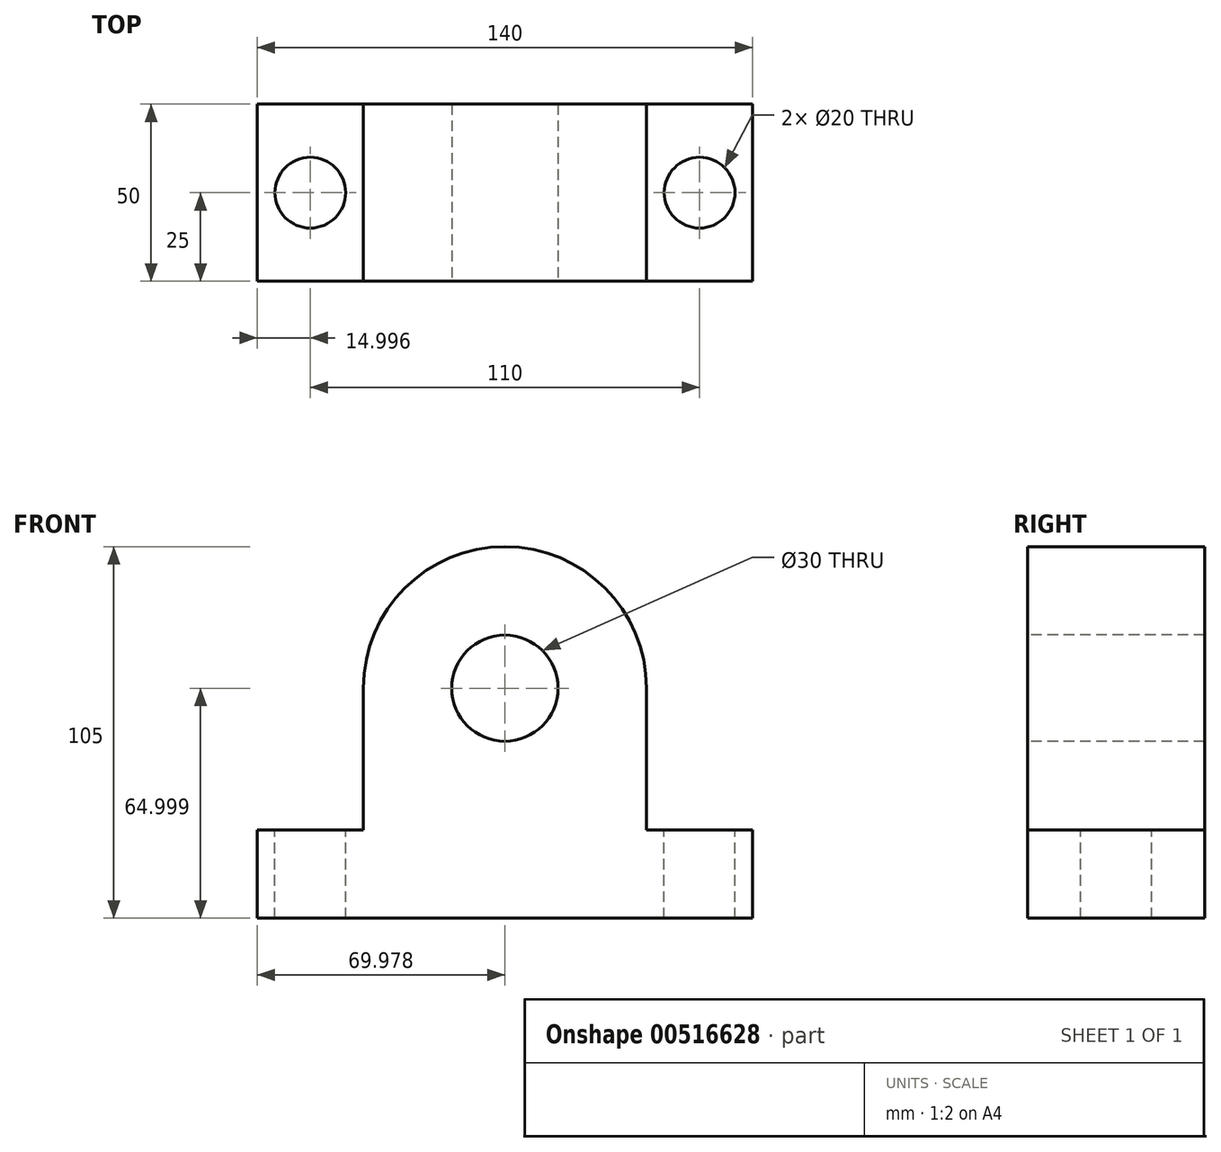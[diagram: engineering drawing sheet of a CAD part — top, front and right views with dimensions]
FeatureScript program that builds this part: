
annotation { "Feature Type Name" : "Feature", "Feature Type Description" : "" }
export const myFeature = defineFeature(function(context is Context, id is Id, definition is map)
    precondition{}
    {
        {
            var Q0;
            Q0=qCreatedBy(makeId("Front.planeOp"),FACE);
            var sketch = newSketch(context, id + "F0", { "sketchPlane" : qUnion([Q0])});
            skLineSegment(sketch, "E0.bottom", {"start": v(-87.17, 37) * mm, "end": v(-57.17, 37) * mm});
            skLineSegment(sketch, "E0.top", {"start": v(-87.17, 12) * mm, "end": v(52.83, 12) * mm});
            skLineSegment(sketch, "E0.left", {"start": v(-87.17, 37) * mm, "end": v(-87.17, 12) * mm});
            skLineSegment(sketch, "E0.right", {"start": v(52.83, 37) * mm, "end": v(52.83, 12) * mm});
            skLineSegment(sketch, "E1.left", {"start": v(-57.17, 77) * mm, "end": v(-57.17, 37) * mm});
            skLineSegment(sketch, "E1.right", {"start": v(22.83, 77) * mm, "end": v(22.83, 37) * mm});
            skLineSegment(sketch, "E2.trimOffspring", {"start": v(22.83, 37) * mm, "end": v(52.83, 37) * mm});
            skArc(sketch, "E3", {"start": v(22.83, 77) * mm, "mid": v(-17.17, 117) * mm, "end": v(-57.17, 77) * mm});
            skSolve(sketch);
        }
        {
            var Q0;
            Q0 = qSketchRegion(id + "F0", true);
            extrude(context, id + "F1", {"entities" : qUnion([Q0]), "depth" : 50 * mm, "offsetDistance" : 25 * mm});
        }
        {
            var Q0;
            Q0=makeQuery(id+"F1.opExtrude","CAP_FACE",FACE,{"disambiguationData":[OSD([sQuery(id+"F0.wireOp",EDGE,"E0.bottom"),sQuery(id+"F0.wireOp",EDGE,"E0.top"),sQuery(id+"F0.wireOp",EDGE,"E0.left"),sQuery(id+"F0.wireOp",EDGE,"E0.right"),sQuery(id+"F0.wireOp",EDGE,"E1.left"),sQuery(id+"F0.wireOp",EDGE,"E1.right"),sQuery(id+"F0.wireOp",EDGE,"E2.trimOffspring"),sQuery(id+"F0.wireOp",EDGE,"E3")])],"isStart":false});
            var sketch = newSketch(context, id + "F2", { "sketchPlane" : qUnion([Q0])});
            skCircle(sketch, "E4", {"center": v(-17.2, 77) * mm, "radius": 15 * mm});
            skSolve(sketch);
        }
        {
            var Q0;
            Q0 = qSketchRegion(id + "F2", true);
            extrude(context, id + "F3", {"entities" : qUnion([Q0]), "operationType" : NewBodyOperationType.REMOVE, "oppositeDirection" : true, "depth" : 51 * mm, "offsetDistance" : 25 * mm});
        }
        {
            var Q0;
            Q0=makeQuery(id+"F1.opExtrude","SWEPT_FACE",FACE,{"disambiguationData":[OSD([sQuery(id+"F0.wireOp",EDGE,"E0.bottom")])]});
            var sketch = newSketch(context, id + "F4", { "sketchPlane" : qUnion([Q0])});
            skCircle(sketch, "E5", {"center": v(-72.17, -25) * mm, "radius": 10 * mm});
            skCircle(sketch, "E6", {"center": v(37.83, -25) * mm, "radius": 10 * mm});
            skSolve(sketch);
        }
        {
            var Q0;
            Q0 = qSketchRegion(id + "F4", true);
            extrude(context, id + "F5", {"entities" : qUnion([Q0]), "operationType" : NewBodyOperationType.REMOVE, "oppositeDirection" : true, "depth" : 51 * mm, "offsetDistance" : 25 * mm});
        }
    });
